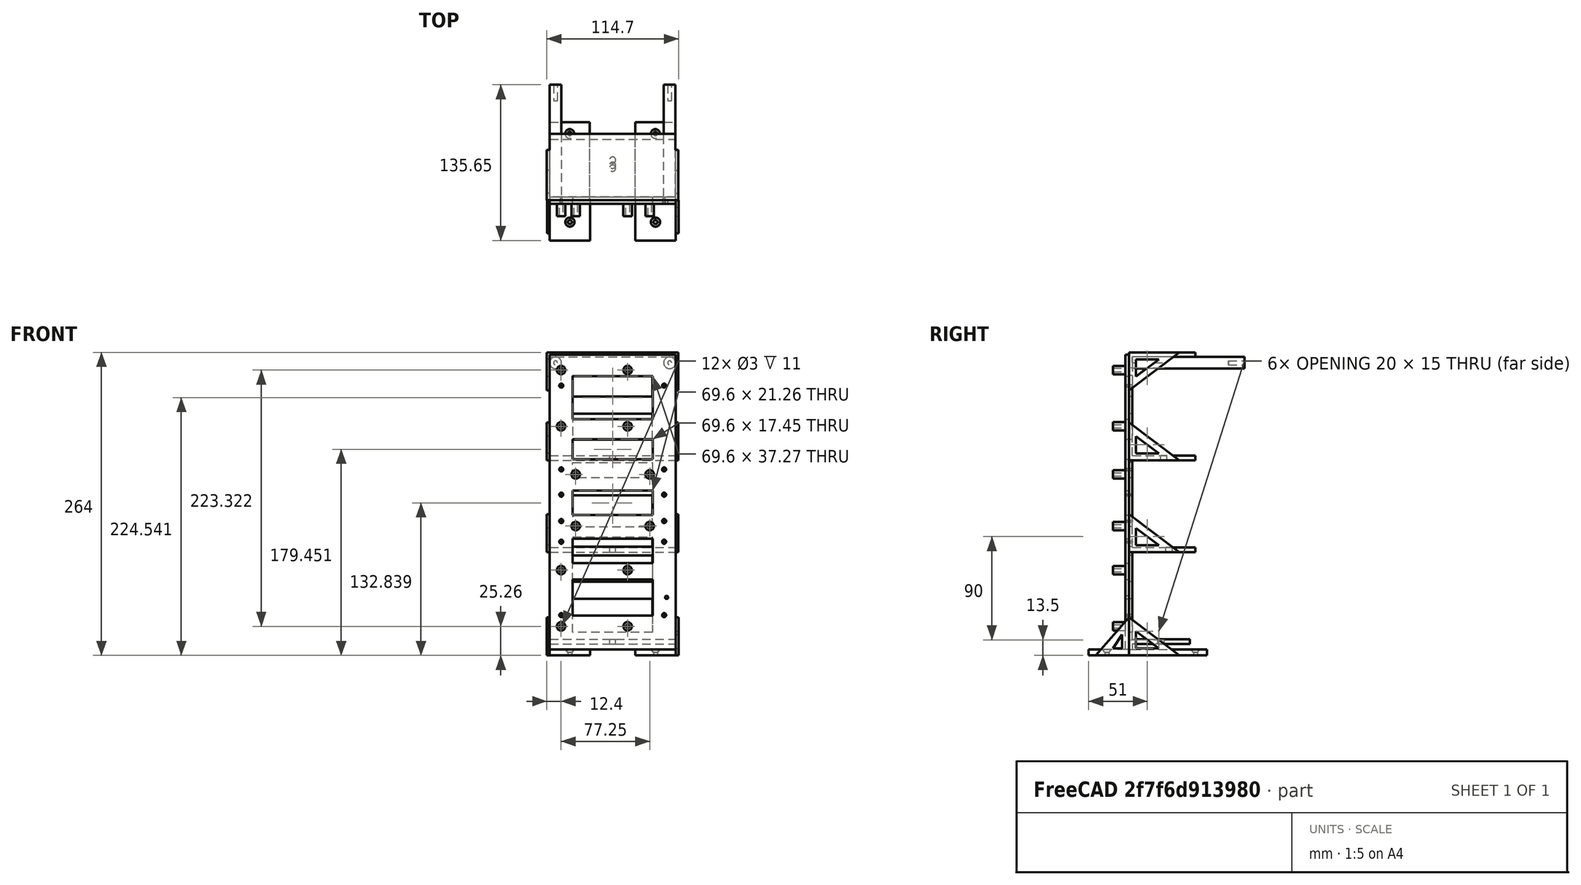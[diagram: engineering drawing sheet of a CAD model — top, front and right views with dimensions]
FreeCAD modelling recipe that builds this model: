
FCSTD DOCUMENT  (FreeCAD 1.0R39109 (Git))
Label: Tower
License: All rights reserved
LicenseURL: http://en.wikipedia.org/wiki/All_rights_reserved
objects: Sketcher::SketchObject×17, PartDesign::Pad×9, PartDesign::Plane×9, PartDesign::Pocket×4, App::Link×3, PartDesign::Hole×3, PartDesign::Mirrored×2, PartDesign::Body×2, App::Part×1
note: 97 computed .brp shape members not serialized (recipe doc carries the construction recipe); baked Part::Feature solids carry a one-line shape summary decoded from their .brp
EXTERNAL_REF file=../Master Document.FCStd obj=Spreadsheet
EXTERNAL_REF file=../../../Dev/PiTrac/3D Printed Parts/Enclosure Models/Combined Enclosure Model (DO NOT PRINT)/Connector Board.FCStd obj=GolfSim_Connector_Board_1
EXTERNAL_REF file=../../../Dev/PiTrac/3D Printed Parts/Enclosure Models/Combined Enclosure Model (DO NOT PRINT)/Pi 5.FCStd obj=RASPBERRY_PI_5_1

FEATURE [App::Link] Link  label="Monitor Chassis Parameters"
  LinkedObject = -> <external ../Master Document.FCStd>#Spreadsheet
FEATURE [Sketcher::SketchObject] Sketch  label="Backplate Sketch"
  ArcFitTolerance = 1e-06
  AttachmentSupport = -> [XZ_Plane001]
  FullyConstrained = false
  MakeInternals = false
  MapMode = 5
  Placement = pos=(0,0,0) rot=(1,0,0;1.5708rad)
  expr: Constraints[10] = <<Monitor Chassis Parameters>>.GSBackPlateBoltDiameter
  expr: Constraints[11] = <<Monitor Chassis Parameters>>.GSComputeBoardWidth / 2 - <<Monitor Chassis Parameters>>.GSBackPlateOuterHolesInsetFromSide
  expr: Constraints[15] = <<Monitor Chassis Parameters>>.GSBackPlateWidthIncrement
  expr: Constraints[55] = <<Monitor Chassis Parameters>>.GSBackPlateLengthIncrement
  expr: Constraints[59] = <<Monitor Chassis Parameters>>.GSBackPlateWidth
  expr: Constraints[71] = <<Monitor Chassis Parameters>>.GSBackPlateMinimumSpanWidth
  expr: Constraints[72] = <<Monitor Chassis Parameters>>.GSBackPlateMinimumSpanWidth
  expr: Constraints[7] = <<Monitor Chassis Parameters>>.GSComputeBoardHeight
  expr: Constraints[80] = <<Monitor Chassis Parameters>>.GSBackPlateLengthIncrement
  expr: Constraints[8] = <<Monitor Chassis Parameters>>.GSComputeBoardWidth
  expr: Constraints[9] = <<Monitor Chassis Parameters>>.GSComputeBoardWidth / 2
  sketch-geometry (33):
    g0: LineSegment [constr] StartX=-50.8 StartY=24.4067 StartZ=0 EndX=50.8 EndY=24.4067 EndZ=0
    g1: LineSegment [constr] StartX=50.8 StartY=24.4067 StartZ=0 EndX=50.8 EndY=253.007 EndZ=0
    g2: LineSegment [constr] StartX=50.8 StartY=253.007 StartZ=0 EndX=-50.8 EndY=253.007 EndZ=0
    g3: LineSegment [constr] StartX=-50.8 StartY=253.007 StartZ=0 EndX=-50.8 EndY=24.4067 EndZ=0
    g4: Circle CenterX=46.99 CenterY=45.5 CenterZ=0 NormalX=0 NormalY=0 NormalZ=1 AngleXU=0 Radius=1.4
    g5: LineSegment StartX=-54.8 StartY=257.007 StartZ=0 EndX=-54.8 EndY=20.4067 EndZ=0
    g6: LineSegment [constr] StartX=-54.8 StartY=20.4067 StartZ=0 EndX=54.8 EndY=20.4067 EndZ=0
    g7: LineSegment StartX=34.8 StartY=117.208 StartZ=0 EndX=-34.8 EndY=117.208 EndZ=0
    g8: LineSegment StartX=-34.8 StartY=117.208 StartZ=0 EndX=-34.8 EndY=138.47 EndZ=0
    g9: LineSegment StartX=-34.8 StartY=138.47 StartZ=0 EndX=34.8 EndY=138.47 EndZ=0
    g10: LineSegment StartX=34.8 StartY=138.47 StartZ=0 EndX=34.8 EndY=117.208 EndZ=0
    g11: LineSegment StartX=34.8 StartY=238.176 StartZ=0 EndX=-34.8 EndY=238.176 EndZ=0
    g12: LineSegment StartX=-34.8 StartY=238.176 StartZ=0 EndX=-34.8 EndY=200.906 EndZ=0
    g13: LineSegment StartX=-34.8 StartY=200.906 StartZ=0 EndX=34.8 EndY=200.906 EndZ=0
    g14: LineSegment StartX=34.8 StartY=200.906 StartZ=0 EndX=34.8 EndY=238.176 EndZ=0
    g15: LineSegment StartX=-34.8 StartY=183.174 StartZ=0 EndX=-34.8 EndY=165.729 EndZ=0
    g16: LineSegment StartX=-34.8 StartY=165.729 StartZ=0 EndX=34.8 EndY=165.729 EndZ=0
    g17: LineSegment StartX=34.8 StartY=165.729 StartZ=0 EndX=34.8 EndY=183.174 EndZ=0
    g18: LineSegment StartX=34.8 StartY=183.174 StartZ=0 EndX=-34.8 EndY=183.174 EndZ=0
    g19: LineSegment StartX=-34.8 StartY=96.4911 StartZ=0 EndX=-34.8 EndY=75.4807 EndZ=0
    g20: LineSegment StartX=-34.8 StartY=75.4807 StartZ=0 EndX=34.8 EndY=75.4807 EndZ=0
    g21: LineSegment StartX=34.8 StartY=75.4807 StartZ=0 EndX=34.8 EndY=96.4911 EndZ=0
    g22: LineSegment StartX=34.8 StartY=96.4911 StartZ=0 EndX=-34.8 EndY=96.4911 EndZ=0
    g23: LineSegment StartX=-34.8 StartY=61.1974 StartZ=0 EndX=-34.8 EndY=29.6985 EndZ=0
    g24: LineSegment StartX=34.8 StartY=29.6985 StartZ=0 EndX=34.8 EndY=61.1974 EndZ=0
    g25: LineSegment StartX=54.8 StartY=20.4067 StartZ=0 EndX=54.8 EndY=257.007 EndZ=0
    g26: LineSegment StartX=-54.8 StartY=257.007 StartZ=0 EndX=54.8 EndY=257.007 EndZ=0
    g27: LineSegment StartX=-54.8 StartY=20.4067 StartZ=0 EndX=-54.8 EndY=0 EndZ=0
    g28: LineSegment StartX=-54.8 StartY=0 StartZ=0 EndX=54.8 EndY=0 EndZ=0
    g29: LineSegment StartX=54.8 StartY=0 StartZ=0 EndX=54.8 EndY=20.4067 EndZ=0
    g30: LineSegment [constr] StartX=54.8 StartY=20.4067 StartZ=0 EndX=-54.8 EndY=20.4067 EndZ=0
    g31: LineSegment StartX=-34.8 StartY=61.1974 StartZ=0 EndX=34.8 EndY=61.1974 EndZ=0
    g32: LineSegment StartX=-34.8 StartY=29.6985 StartZ=0 EndX=34.8 EndY=29.6985 EndZ=0
  constraints (86):
    c: Coincident(g0,g1)
    c: Coincident(g1,g2)
    c: Coincident(g2,g3)
    c: Coincident(g3,g0)
    c: Horizontal(g2)
    c: Vertical(g1)
    c: Vertical(g3)
    c: DistanceY(g0,g2) = 228.6
    c: DistanceX(g0,g0) = 101.6
    c: DistanceX(g0,g-1) = 50.8
    c: Diameter(g4) = 2.8
    c: DistanceX(g-1,g4) = 46.99
    c: Coincident(g5,g6)
    c: Vertical(g5)
    c: Horizontal(g6)
    c: DistanceX(g5,g0) = 4
    c: Horizontal(g0)
    c: Coincident(g7,g8)
    c: Coincident(g8,g9)
    c: Coincident(g9,g10)
    c: Coincident(g10,g7)
    c: Horizontal(g7)
    c: Vertical(g8)
    c: Vertical(g10)
    c: Coincident(g11,g12)
    c: Coincident(g12,g13)
    c: Coincident(g13,g14)
    c: Coincident(g14,g11)
    c: Horizontal(g11)
    c: Horizontal(g13)
    c: Vertical(g12)
    c: Vertical(g14)
    c: Coincident(g15,g16)
    c: Coincident(g16,g17)
    c: Coincident(g17,g18)
    c: Coincident(g18,g15)
    c: Vertical(g15)
    c: Vertical(g17)
    c: Horizontal(g16)
    c: Coincident(g19,g20)
    c: Coincident(g20,g21)
    c: Coincident(g21,g22)
    c: Coincident(g22,g19)
    c: Vertical(g19)
    c: Vertical(g21)
    c: Horizontal(g20)
    c: Horizontal(g22)
    c: Vertical(g23)
    c: Vertical(g24)
    c: Vertical(g15,g19)
    c: Vertical(g19,g23)
    c: Vertical(g7,g21)
    c: Vertical(g21,g24)
    c: Coincident(g25,g6)
    c: Vertical(g25)
    c: DistanceY(g1,g25) = 4
    c: Horizontal(g5,g25)
    c: Coincident(g26,g5)
    c: Coincident(g26,g25)
    c: DistanceX(g5,g6) = 109.6
    c: Coincident(g27,g28)
    c: Coincident(g28,g29)
    c: Coincident(g29,g30)
    c: Coincident(g30,g27)
    c: Vertical(g27)
    c: Vertical(g29)
    c: Horizontal(g28)
    c: Horizontal(g30)
    c: Coincident(g27,g5)
    c: Horizontal(g28,g-1)
    c: Vertical(g29,g6)
    c: DistanceX(g5,g11) = 20
    c: DistanceX(g11,g25) = 20
    c: Horizontal(g9)
    c: Coincident(g31,g23)
    c: Coincident(g31,g24)
    c: Horizontal(g31)
    c: Vertical(g11,g15)
    c: Vertical(g11,g9)
    c: Vertical(g16,g9)
    c: DistanceY(g5,g0) = 4
    c: Coincident(g32,g23)
    c: Coincident(g32,g24)
    c: Horizontal(g32)
    c: Horizontal(g18)
    c: Vertical(g15,g8)
FEATURE [PartDesign::Pad] Pad  label="Backplate Pad"
  Direction = (0,-1,2e-16)
  Length = 3
  Length2 = 10
  Placement = pos=(0,0,0) rot=(1,0,0;1.5708rad)
  Profile = -> Sketch
  ReferenceAxis = -> Sketch [N_Axis]
  Reversed = true
  Suppressed = false
  Type = 0
  expr: Length = <<Monitor Chassis Parameters>>.GSBackPlateThickness
FEATURE [Sketcher::SketchObject] Sketch001  label="Backplate Risers Sketch"
  ArcFitTolerance = 1e-06
  AttachmentSupport = -> [XZ_Plane001]
  FullyConstrained = false
  MakeInternals = false
  MapMode = 5
  Placement = pos=(0,0,0) rot=(1,0,0;1.5708rad)
  expr: Constraints[10] = <<Monitor Chassis Parameters>>.GsPi5MountingHoleDiameter
  expr: Constraints[11] = <<Monitor Chassis Parameters>>.GsPi5MountingHoleDiameter
  expr: Constraints[12] = <<Monitor Chassis Parameters>>.GsPi5MountingHoleDiameter
  expr: Constraints[13] = <<Monitor Chassis Parameters>>.GsPi5MountingHoleDiameter
  expr: Constraints[18] = <<Monitor Chassis Parameters>>.GSBackPlateScrewHoleDiameter + 2 * <<Monitor Chassis Parameters>>.GSBackPlateStandoffWallThickness
  expr: Constraints[20] = <<Monitor Chassis Parameters>>.GSBackPlateScrewHoleDiameter + 2 * <<Monitor Chassis Parameters>>.GSBackPlateStandoffWallThickness
  expr: Constraints[26] = <<Monitor Chassis Parameters>>.GSBackPlateScrewHoleDiameter + 2 * <<Monitor Chassis Parameters>>.GSBackPlateStandoffWallThickness
  expr: Constraints[27] = <<Monitor Chassis Parameters>>.GSBackPlateScrewHoleDiameter + 2 * <<Monitor Chassis Parameters>>.GSBackPlateStandoffWallThickness
  expr: Constraints[28] = <<Monitor Chassis Parameters>>.GSBackPlateScrewHoleDiameter + 2 * <<Monitor Chassis Parameters>>.GSBackPlateStandoffWallThickness
  expr: Constraints[29] = <<Monitor Chassis Parameters>>.GSBackPlateScrewHoleDiameter + 2 * <<Monitor Chassis Parameters>>.GSBackPlateStandoffWallThickness
  expr: Constraints[30] = <<Monitor Chassis Parameters>>.GSBackPlateScrewHoleDiameter + 2 * <<Monitor Chassis Parameters>>.GSBackPlateStandoffWallThickness
  expr: Constraints[32] = <<Monitor Chassis Parameters>>.GSBackPlateVerticalOffset
  expr: Constraints[34] = <<Monitor Chassis Parameters>>.GSPi5MountingHoleCenterLength
  expr: Constraints[36] = <<Monitor Chassis Parameters>>.GSPi5MountingHoleCenterWidth
  expr: Constraints[38] = <<Monitor Chassis Parameters>>.GSPi5MountingHoleCenterWidth
  expr: Constraints[41] = <<Monitor Chassis Parameters>>.GsPi5MountingHoleDiameter
  expr: Constraints[58] = <<Monitor Chassis Parameters>>.GSMonitorConnectorBoardHoleSeparationLength
  expr: Constraints[59] = <<Monitor Chassis Parameters>>.GSMonitorConnectorBoardHoleSeparationWidth
  expr: Constraints[60] = 0.5 * <<Monitor Chassis Parameters>>.GSMonitorConnectorBoardHoleSeparationLength
  expr: Constraints[61] = <<Monitor Chassis Parameters>>.GSPi5MountingHoleCenterLength
  expr: Constraints[6] = <<Monitor Chassis Parameters>>.GSComputeBoardWidth / 2
  expr: Constraints[7] = <<Monitor Chassis Parameters>>.GsPi5MountingHoleDiameter
  expr: Constraints[8] = <<Monitor Chassis Parameters>>.GsPi5MountingHoleDiameter
  expr: Constraints[9] = <<Monitor Chassis Parameters>>.GsPi5MountingHoleDiameter
  sketch-geometry (28):
    g0: LineSegment [constr] StartX=-50.8 StartY=20 StartZ=0 EndX=50.8 EndY=20 EndZ=0
    g1: LineSegment [constr] StartX=50.8 StartY=20 StartZ=0 EndX=50.8 EndY=248.6 EndZ=0
    g2: LineSegment [constr] StartX=50.8 StartY=248.6 StartZ=0 EndX=-50.8 EndY=248.6 EndZ=0
    g3: LineSegment [constr] StartX=-50.8 StartY=248.6 StartZ=0 EndX=-50.8 EndY=20 EndZ=0
    g4: Circle CenterX=-45 CenterY=243.582 CenterZ=0 NormalX=0 NormalY=0 NormalZ=1 AngleXU=0 Radius=1.5
    g5: Circle CenterX=13 CenterY=243.582 CenterZ=0 NormalX=0 NormalY=0 NormalZ=1 AngleXU=0 Radius=1.5
    g6: Circle CenterX=-45 CenterY=20.2601 CenterZ=0 NormalX=0 NormalY=0 NormalZ=1 AngleXU=0 Radius=1.5
    g7: Circle CenterX=13 CenterY=20.2601 CenterZ=0 NormalX=0 NormalY=0 NormalZ=1 AngleXU=0 Radius=1.5
    g8: Circle CenterX=-45 CenterY=69.2601 CenterZ=0 NormalX=0 NormalY=0 NormalZ=1 AngleXU=0 Radius=1.5
    g9: Circle CenterX=-45 CenterY=194.582 CenterZ=0 NormalX=0 NormalY=0 NormalZ=1 AngleXU=0 Radius=1.5
    g10: Circle CenterX=13 CenterY=194.582 CenterZ=0 NormalX=0 NormalY=0 NormalZ=1 AngleXU=0 Radius=1.5
    g11: Circle CenterX=-45 CenterY=243.582 CenterZ=0 NormalX=0 NormalY=0 NormalZ=1 AngleXU=0 Radius=3.7
    g12: Circle CenterX=13 CenterY=243.582 CenterZ=0 NormalX=0 NormalY=0 NormalZ=1 AngleXU=0 Radius=3.7
    g13: Circle CenterX=-45 CenterY=194.582 CenterZ=0 NormalX=0 NormalY=0 NormalZ=1 AngleXU=0 Radius=3.7
    g14: Circle CenterX=13 CenterY=194.582 CenterZ=0 NormalX=0 NormalY=0 NormalZ=1 AngleXU=0 Radius=3.7
    g15: Circle CenterX=-45 CenterY=69.2601 CenterZ=0 NormalX=0 NormalY=0 NormalZ=1 AngleXU=0 Radius=3.7
    g16: Circle CenterX=-45 CenterY=20.2601 CenterZ=0 NormalX=0 NormalY=0 NormalZ=1 AngleXU=0 Radius=3.7
    g17: Circle CenterX=13 CenterY=20.2601 CenterZ=0 NormalX=0 NormalY=0 NormalZ=1 AngleXU=0 Radius=3.7
    g18: Circle CenterX=13 CenterY=69.2601 CenterZ=0 NormalX=0 NormalY=0 NormalZ=1 AngleXU=0 Radius=3.7
    g19: Circle CenterX=13 CenterY=69.2601 CenterZ=0 NormalX=0 NormalY=0 NormalZ=1 AngleXU=0 Radius=1.5
    g20: Circle CenterX=-32.25 CenterY=107.639 CenterZ=0 NormalX=0 NormalY=0 NormalZ=1 AngleXU=0 Radius=1.5
    g21: Circle CenterX=-32.25 CenterY=107.639 CenterZ=0 NormalX=0 NormalY=0 NormalZ=1 AngleXU=0 Radius=3.7
    g22: Circle CenterX=32.25 CenterY=107.639 CenterZ=0 NormalX=0 NormalY=0 NormalZ=1 AngleXU=0 Radius=1.5
    g23: Circle CenterX=32.25 CenterY=107.639 CenterZ=0 NormalX=0 NormalY=0 NormalZ=1 AngleXU=0 Radius=3.7
    g24: Circle CenterX=32.25 CenterY=152.639 CenterZ=0 NormalX=0 NormalY=0 NormalZ=1 AngleXU=0 Radius=1.5
    g25: Circle CenterX=32.25 CenterY=152.639 CenterZ=0 NormalX=0 NormalY=0 NormalZ=1 AngleXU=0 Radius=3.7
    g26: Circle CenterX=-32.25 CenterY=152.639 CenterZ=0 NormalX=0 NormalY=0 NormalZ=1 AngleXU=0 Radius=1.5
    g27: Circle CenterX=-32.25 CenterY=152.639 CenterZ=0 NormalX=0 NormalY=0 NormalZ=1 AngleXU=0 Radius=3.7
  constraints (65):
    c: Coincident(g0,g1)
    c: Coincident(g1,g2)
    c: Coincident(g2,g3)
    c: Coincident(g3,g0)
    c: Vertical(g1)
    c: Vertical(g3)
    c: DistanceX(g0,g-1) = 50.8
    c: Diameter(g4) = 3
    c: Diameter(g5) = 3
    c: Diameter(g6) = 3
    c: Diameter(g7) = 3
    c: Diameter(g8) = 3
    c: Diameter(g9) = 3
    c: Diameter(g10) = 3
    c: Horizontal(g0)
    c: Vertical(g5,g10)
    c: Horizontal(g5,g4)
    c: Coincident(g11,g4)
    c: Diameter(g11) = 7.4
    c: Coincident(g12,g5)
    c: Diameter(g12) = 7.4
    c: Coincident(g13,g9)
    c: Coincident(g14,g10)
    c: Coincident(g15,g8)
    c: Coincident(g16,g6)
    c: Coincident(g17,g7)
    c: Diameter(g17) = 7.4
    c: Diameter(g16) = 7.4
    c: Diameter(g15) = 7.4
    c: Diameter(g14) = 7.4
    c: Diameter(g13) = 7.4
    c: Horizontal(g7,g6)
    c: DistanceY(g-1,g0) = 20
    c: Horizontal(g2,g1)
    c: DistanceX(g4,g5) = 58
    c: Horizontal(g9,g10)
    c: DistanceY(g9,g4) = 49
    c: Vertical(g8,g6)
    c: DistanceY(g6,g8) = 49
    c: Diameter(g18) = 7.4
    c: Coincident(g19,g18)
    c: Diameter(g19) = 3
    c: Horizontal(g18,g8)
    c: Vertical(g18,g7)
    c: Coincident(g21,g20)
    c: Diameter(g21) = 7.4
    c: Diameter(g20) = 3
    c: Coincident(g23,g22)
    c: Diameter(g23) = 7.4
    c: Diameter(g22) = 3
    c: Coincident(g25,g24)
    c: Diameter(g25) = 7.4
    c: Diameter(g24) = 3
    c: Coincident(g27,g26)
    c: Diameter(g27) = 7.4
    c: Diameter(g26) = 3
    c: Horizontal(g24,g26)
    c: Horizontal(g22,g20)
    c: DistanceX(g26,g24) = 64.5
    c: DistanceY(g20,g26) = 45
    c: DistanceX(g26,g-1) = 32.25
    c: DistanceX(g8,g18) = 58
    c: DistanceX(g6,g-1) = 45
    c: Vertical(g8,g9)
    c: Vertical(g10,g7)
FEATURE [PartDesign::Pad] Pad001  label="Backplate Risers Pad"
  BaseFeature = -> Pad
  Direction = (0,-1,2e-16)
  Length = 11
  Length2 = 10
  Placement = pos=(0,0,0) rot=(1,0,0;1.5708rad)
  Profile = -> Sketch001
  ReferenceAxis = -> Sketch001 [N_Axis]
  Suppressed = false
  Type = 0
  expr: Length = <<Monitor Chassis Parameters>>.GSBackPlateStandoffHeight
FEATURE [Sketcher::SketchObject] Sketch002  label="Backplate Foot Sketch"
  ArcFitTolerance = 1e-06
  AttachmentSupport = -> [XZ_Plane001]
  FullyConstrained = true
  MakeInternals = false
  MapMode = 5
  Placement = pos=(0,0,0) rot=(1,0,0;1.5708rad)
  expr: Constraints[11] = <<Monitor Chassis Parameters>>.GSTowerFeetThickness
  expr: Constraints[21] = <<Monitor Chassis Parameters>>.GSTowerFeetThickness
  expr: Constraints[22] = <<Monitor Chassis Parameters>>.GSBackPlateFootWidth
  expr: Constraints[23] = 0.5 * <<Monitor Chassis Parameters>>.GSBackPlateWidth
  expr: Constraints[8] = <<Monitor Chassis Parameters>>.GSBackPlateFootWidth
  expr: Constraints[9] = 0.5 * <<Monitor Chassis Parameters>>.GSBackPlateWidth
  sketch-geometry (8):
    g0: LineSegment StartX=-54.8 StartY=-5 StartZ=0 EndX=-19.8 EndY=-5 EndZ=0
    g1: LineSegment StartX=-19.8 StartY=-5 StartZ=0 EndX=-19.8 EndY=0 EndZ=0
    g2: LineSegment StartX=-19.8 StartY=0 StartZ=0 EndX=-54.8 EndY=0 EndZ=0
    g3: LineSegment StartX=-54.8 StartY=0 StartZ=0 EndX=-54.8 EndY=-5 EndZ=0
    g4: LineSegment StartX=54.8 StartY=-5 StartZ=0 EndX=54.8 EndY=0 EndZ=0
    g5: LineSegment StartX=54.8 StartY=0 StartZ=0 EndX=19.8 EndY=0 EndZ=0
    g6: LineSegment StartX=19.8 StartY=0 StartZ=0 EndX=19.8 EndY=-5 EndZ=0
    g7: LineSegment StartX=19.8 StartY=-5 StartZ=0 EndX=54.8 EndY=-5 EndZ=0
  constraints (24):
    c: Coincident(g0,g1)
    c: Coincident(g1,g2)
    c: Coincident(g2,g3)
    c: Coincident(g3,g0)
    c: Horizontal(g0)
    c: Horizontal(g2)
    c: Vertical(g1)
    c: Vertical(g3)
    c: DistanceX(g2,g1) = 35
    c: DistanceX(g2,g-1) = 54.8
    c: Horizontal(g2,g-1)
    c: DistanceY(g0,g2) = 5
    c: Coincident(g4,g5)
    c: Coincident(g5,g6)
    c: Coincident(g6,g7)
    c: Coincident(g7,g4)
    c: Vertical(g4)
    c: Vertical(g6)
    c: Horizontal(g5)
    c: Horizontal(g7)
    c: Horizontal(g5,g-1)
    c: DistanceY(g4,g4) = 5
    c: DistanceX(g6,g4) = 35
    c: DistanceX(g-1,g4) = 54.8
FEATURE [PartDesign::Pad] Pad002  label="Backplate Foot Pad"
  BaseFeature = -> Pad001
  Direction = (0,-1,2e-16)
  Length = 32
  Length2 = 3
  Placement = pos=(0,0,0) rot=(1,0,0;1.5708rad)
  Profile = -> Sketch002
  ReferenceAxis = -> Sketch002 [N_Axis]
  Suppressed = false
  Type = 4
  expr: Length = <<Monitor Chassis Parameters>>.GSBackPlateFootLengthBackward
  expr: Length2 = <<Monitor Chassis Parameters>>.GSBackPlateThickness
FEATURE [Sketcher::SketchObject] Sketch003  label="Backplate Foot Screw Holes Sketch"
  ArcFitTolerance = 1e-06
  AttachmentSupport = -> [XY_Plane001]
  FullyConstrained = true
  MakeInternals = false
  MapMode = 5
  expr: Constraints[0] = 0.5 * <<Monitor Chassis Parameters>>.GSBackPlateFootLengthBackward
  expr: Constraints[1] = 0.5 * <<Monitor Chassis Parameters>>.GSBackPlateWidth - 0.5 * <<Monitor Chassis Parameters>>.GSBackPlateFootWidth
  expr: Constraints[2] = 0.5 * <<Monitor Chassis Parameters>>.GSBackPlateWidth - 0.5 * <<Monitor Chassis Parameters>>.GSBackPlateFootWidth
  expr: Constraints[3] = <<Monitor Chassis Parameters>>.GSTowerFeetScrewDiameter
  expr: Constraints[4] = <<Monitor Chassis Parameters>>.GSTowerFeetScrewDiameter
  sketch-geometry (2):
    g0: Circle CenterX=-37.3 CenterY=-16 CenterZ=0 NormalX=0 NormalY=0 NormalZ=1 AngleXU=0 Radius=1.7
    g1: Circle CenterX=37.3 CenterY=-16 CenterZ=0 NormalX=0 NormalY=0 NormalZ=1 AngleXU=0 Radius=1.7
  constraints (6):
    c: DistanceY(g0,g-1) = 16
    c: DistanceX(g0,g-1) = 37.3
    c: DistanceX(g-1,g1) = 37.3
    c: Diameter(g0) = 3.4
    c: Diameter(g1) = 3.4
    c: Horizontal(g1,g0)
FEATURE [PartDesign::Hole] Hole  label="Backplate Foot Screw Holes"
  BaseFeature = -> Pad002
  CustomThreadClearance = 0
  Depth = 25
  DepthType = 0
  Diameter = 3.4
  DrillForDepth = false
  DrillPoint = 1
  DrillPointAngle = 118
  HoleCutCountersinkAngle = 90
  HoleCutCustomValues = false
  HoleCutDepth = 0
  HoleCutDiameter = 8
  HoleCutType = 2
  ModelThread = false
  Placement = pos=(0,0,0) rot=(1,0,0;1.5708rad)
  Profile = -> Sketch003
  Suppressed = false
  Tapered = false
  TaperedAngle = 90
  ThreadClass = 0
  ThreadDepth = 25
  ThreadDepthType = 0
  ThreadDirection = 0
  ThreadFit = 0
  ThreadSize = 0
  ThreadType = 0
  Threaded = false
  UseCustomThreadClearance = false
  expr: Diameter = <<Monitor Chassis Parameters>>.GSTowerFeetScrewDiameter
  expr: HoleCutDiameter = <<Monitor Chassis Parameters>>.GSM4BoltCountersinkDiameter
FEATURE [PartDesign::Plane] DatumPlane
  AttachmentOffset = pos=(0,0,54.8) rot=(0,0,1;0rad)
  AttachmentSupport = -> [YZ_Plane001]
  Length = 82.357
  MapMode = 5
  Placement = pos=(54.8,0,0) rot=(0.57735,0.57735,0.57735;2.0944rad)
  ResizeMode = 0
  Width = 307.364
  expr: .AttachmentOffset.Base.z = 0.5 * <<Monitor Chassis Parameters>>.GSBackPlateWidth
FEATURE [Sketcher::SketchObject] Sketch004  label="Foot Support Corner Sketch"
  ArcFitTolerance = 1e-06
  AttachmentSupport = -> [DatumPlane]
  FullyConstrained = true
  MakeInternals = false
  MapMode = 5
  Placement = pos=(54.8,0,0) rot=(0.57735,0.57735,0.57735;2.0944rad)
  expr: Constraints[14] = <<Monitor Chassis Parameters>>.GSSideCornerCutoutInset
  expr: Constraints[15] = <<Monitor Chassis Parameters>>.GSSideCornerCutoutInset
  expr: Constraints[16] = 2.5 * <<Monitor Chassis Parameters>>.GSSideCornerCutoutInset
  expr: Constraints[17] = 2.5 * <<Monitor Chassis Parameters>>.GSSideCornerCutoutInset
  expr: Constraints[1] = <<Monitor Chassis Parameters>>.GSBackPlateThickness
  expr: Constraints[4] = <<Monitor Chassis Parameters>>.GSTowerFeetThickness
  expr: Constraints[7] = 0.9 * <<Monitor Chassis Parameters>>.GSBackPlateFootLengthBackward
  expr: Constraints[8] = 0.6 * <<Monitor Chassis Parameters>>.GSTowerFloorDepth
  sketch-geometry (6):
    g0: LineSegment StartX=-25.8 StartY=-5 StartZ=0 EndX=3 EndY=-5 EndZ=0
    g1: LineSegment StartX=3 StartY=28 StartZ=0 EndX=3 EndY=-5 EndZ=0
    g2: LineSegment StartX=-25.8 StartY=-5 StartZ=0 EndX=3 EndY=28 EndZ=0
    g3: LineSegment StartX=-10.8 StartY=1 StartZ=0 EndX=-3 EndY=13 EndZ=0
    g4: LineSegment StartX=-3 StartY=13 StartZ=0 EndX=-3 EndY=1 EndZ=0
    g5: LineSegment StartX=-10.8 StartY=1 StartZ=0 EndX=-3 EndY=1 EndZ=0
  constraints (18):
    c: Horizontal(g0)
    c: DistanceX(g-1,g0) = 3
    c: Coincident(g1,g0)
    c: Vertical(g1)
    c: DistanceY(g0,g-1) = 5
    c: Coincident(g2,g0)
    c: Coincident(g2,g1)
    c: DistanceX(g0,g0) = 28.8
    c: DistanceY(g0,g1) = 33
    c: Coincident(g4,g3)
    c: Vertical(g4)
    c: Coincident(g5,g3)
    c: Coincident(g5,g4)
    c: Horizontal(g5)
    c: DistanceY(g0,g4) = 6
    c: DistanceX(g4,g0) = 6
    c: DistanceX(g0,g3) = 15
    c: DistanceY(g3,g1) = 15
FEATURE [PartDesign::Pad] Pad003  label="Foot Support Corner Pad"
  BaseFeature = -> Hole
  Direction = (1,0,0)
  Length = 2.5
  Length2 = 10
  Placement = pos=(0,0,0) rot=(1,0,0;1.5708rad)
  Profile = -> Sketch004
  ReferenceAxis = -> Sketch004 [N_Axis]
  Suppressed = false
  Type = 0
  expr: Length = <<Monitor Chassis Parameters>>.GSSideCornerThickness
FEATURE [PartDesign::Mirrored] Mirrored  label="Foot Support Corner Mirrored"
  BaseFeature = -> Pad003
  MirrorPlane = -> YZ_Plane001
  Originals = -> [Pad003]
  Placement = pos=(0,0,0) rot=(1,0,0;1.5708rad)
  Suppressed = false
  TransformMode = 0
FEATURE [PartDesign::Plane] DatumPlane001
  AttachmentOffset = pos=(0,0,54.8) rot=(0,0,1;0rad)
  AttachmentSupport = -> [YZ_Plane002]
  Length = 121.975
  MapMode = 5
  Placement = pos=(54.8,0,0) rot=(0.57735,0.57735,0.57735;2.0944rad)
  ResizeMode = 0
  Width = 315.975
  expr: .AttachmentOffset.Base.z = 0.5 * <<Monitor Chassis Parameters>>.GSBackPlateWidth
FEATURE [Sketcher::SketchObject] Sketch005  label="Frontplate Sketch"
  ArcFitTolerance = 1e-06
  AttachmentSupport = -> [XZ_Plane002]
  FullyConstrained = false
  MakeInternals = false
  MapMode = 5
  Placement = pos=(0,0,0) rot=(1,0,0;1.5708rad)
  expr: Constraints[105] = <<Monitor Chassis Parameters>>.GSFrontPlateMinimumSpanWidth - 5
  expr: Constraints[106] = <<Monitor Chassis Parameters>>.GSTowerFourthFloorHeight + <<Monitor Chassis Parameters>>.GSTowerFloorThickness
  expr: Constraints[107] = <<Monitor Chassis Parameters>>.GSTowerLayerJoinScrewDiameter
  expr: Constraints[108] = <<Monitor Chassis Parameters>>.GSTowerLayerJoinScrewDiameter
  expr: Constraints[110] = <<Monitor Chassis Parameters>>.GSTowerLayerJoinScrewInset
  expr: Constraints[111] = <<Monitor Chassis Parameters>>.GSTowerLayerJoinScrewInset
  expr: Constraints[112] = <<Monitor Chassis Parameters>>.GSTowerLayerJoinScrewDiameter
  expr: Constraints[113] = <<Monitor Chassis Parameters>>.GSTowerLayerJoinScrewDiameter
  expr: Constraints[115] = <<Monitor Chassis Parameters>>.GSTowerLayerJoinScrewDiameter
  expr: Constraints[116] = <<Monitor Chassis Parameters>>.GSTowerLayerJoinScrewDiameter
  expr: Constraints[120] = <<Monitor Chassis Parameters>>.GSTowerLayerJoinScrewDiameter
  expr: Constraints[121] = <<Monitor Chassis Parameters>>.GSTowerLayerJoinScrewDiameter
  expr: Constraints[123] = <<Monitor Chassis Parameters>>.GSTowerLayerJoinScrewHeightFromFoot_1
  expr: Constraints[124] = <<Monitor Chassis Parameters>>.GSTowerLayerJoinScrewHeightFromFoot_3
  expr: Constraints[126] = <<Monitor Chassis Parameters>>.GSTowerLayerJoinScrewHeightFromFoot_4
  expr: Constraints[127] = <<Monitor Chassis Parameters>>.GSTowerLayerJoinScrewHeightFromFoot_5
  expr: Constraints[129] = <<Monitor Chassis Parameters>>.GSTowerLayerJoinScrewDiameter
  expr: Constraints[130] = <<Monitor Chassis Parameters>>.GSTowerLayerJoinScrewDiameter
  expr: Constraints[133] = <<Monitor Chassis Parameters>>.GSTowerLayerJoinScrewHeightFromFoot_6
  expr: Constraints[13] = <<Monitor Chassis Parameters>>.GSBackPlateWidthIncrement
  expr: Constraints[145] = <<Monitor Chassis Parameters>>.GSTowerLayerJoinScrewDiameter
  expr: Constraints[150] = <<Monitor Chassis Parameters>>.GSTowerLayerJoinScrewHeightFromFoot_2
  expr: Constraints[46] = <<Monitor Chassis Parameters>>.GSFrontPlateMinimumSpanWidth - 5
  expr: Constraints[48] = <<Monitor Chassis Parameters>>.GSFrontPlateMinimumSpanWidth
  expr: Constraints[65] = <<Monitor Chassis Parameters>>.GSFrontPlateMinimumSpanWidth - 5
  expr: Constraints[71] = <<Monitor Chassis Parameters>>.GSBackPlateLengthIncrement
  expr: Constraints[75] = <<Monitor Chassis Parameters>>.GSBackPlateWidth
  expr: Constraints[76] = <<Monitor Chassis Parameters>>.GSBackPlateVerticalOffset
  expr: Constraints[7] = <<Monitor Chassis Parameters>>.GSComputeBoardHeight
  expr: Constraints[8] = <<Monitor Chassis Parameters>>.GSComputeBoardWidth
  expr: Constraints[96] = <<Monitor Chassis Parameters>>.GSFrontPlateMinimumSpanWidth - 5
  expr: Constraints[97] = <<Monitor Chassis Parameters>>.GSFrontPlateMinimumSpanWidth
  expr: Constraints[98] = <<Monitor Chassis Parameters>>.GSFrontPlateMinimumSpanWidth
  expr: Constraints[9] = <<Monitor Chassis Parameters>>.GSComputeBoardWidth / 2
  sketch-geometry (55):
    g0: LineSegment [constr] StartX=-50.8 StartY=24 StartZ=0 EndX=50.8 EndY=24 EndZ=0
    g1: LineSegment [constr] StartX=50.8 StartY=24 StartZ=0 EndX=50.8 EndY=252.6 EndZ=0
    g2: LineSegment [constr] StartX=50.8 StartY=252.6 StartZ=0 EndX=-50.8 EndY=252.6 EndZ=0
    g3: LineSegment [constr] StartX=-50.8 StartY=252.6 StartZ=0 EndX=-50.8 EndY=24 EndZ=0
    g4: LineSegment StartX=-54.8 StartY=256.6 StartZ=0 EndX=-54.8 EndY=20 EndZ=0
    g5: LineSegment [constr] StartX=-54.8 StartY=20 StartZ=0 EndX=54.8 EndY=20 EndZ=0
    g6: LineSegment StartX=34.8 StartY=162.959 StartZ=0 EndX=-34.8 EndY=162.959 EndZ=0
    g7: LineSegment StartX=-34.8 StartY=162.959 StartZ=0 EndX=-34.8 EndY=149.512 EndZ=0
    g8: LineSegment StartX=-34.8 StartY=149.512 StartZ=0 EndX=34.8 EndY=149.512 EndZ=0
    g9: LineSegment StartX=34.8 StartY=149.512 StartZ=0 EndX=34.8 EndY=162.959 EndZ=0
    g10: LineSegment StartX=34.8 StartY=107.062 StartZ=0 EndX=-34.8 EndY=107.062 EndZ=0
    g11: LineSegment StartX=-34.8 StartY=107.062 StartZ=0 EndX=-34.8 EndY=134.512 EndZ=0
    g12: LineSegment StartX=-34.8 StartY=134.512 StartZ=0 EndX=34.8 EndY=134.512 EndZ=0
    g13: LineSegment StartX=34.8 StartY=134.512 StartZ=0 EndX=34.8 EndY=107.062 EndZ=0
    g14: LineSegment StartX=34.8 StartY=239 StartZ=0 EndX=-34.8 EndY=239 EndZ=0
    g15: LineSegment StartX=-34.8 StartY=239 StartZ=0 EndX=-34.8 EndY=220.485 EndZ=0
    g16: LineSegment StartX=-34.8 StartY=220.485 StartZ=0 EndX=34.8 EndY=220.485 EndZ=0
    g17: LineSegment StartX=34.8 StartY=220.485 StartZ=0 EndX=34.8 EndY=239 EndZ=0
    g18: LineSegment StartX=34.8 StartY=182.959 StartZ=0 EndX=-34.8 EndY=182.959 EndZ=0
    g19: LineSegment StartX=-34.8 StartY=182.959 StartZ=0 EndX=-34.8 EndY=205.485 EndZ=0
    g20: LineSegment StartX=-34.8 StartY=205.485 StartZ=0 EndX=34.8 EndY=205.485 EndZ=0
    g21: LineSegment StartX=34.8 StartY=205.485 StartZ=0 EndX=34.8 EndY=182.959 EndZ=0
    g22: LineSegment StartX=-34.8 StartY=81.9803 StartZ=0 EndX=-34.8 EndY=59.2632 EndZ=0
    g23: LineSegment StartX=-34.8 StartY=59.2632 StartZ=0 EndX=34.8 EndY=59.2632 EndZ=0
    g24: LineSegment StartX=34.8 StartY=59.2632 StartZ=0 EndX=34.8 EndY=81.9803 EndZ=0
    g25: LineSegment StartX=34.8 StartY=81.9803 StartZ=0 EndX=-34.8 EndY=81.9803 EndZ=0
    g26: LineSegment StartX=-34.8 StartY=44.2632 StartZ=0 EndX=-34.8 EndY=15 EndZ=0
    g27: LineSegment StartX=-34.8 StartY=15 StartZ=0 EndX=34.8 EndY=15 EndZ=0
    g28: LineSegment StartX=34.8 StartY=15 StartZ=0 EndX=34.8 EndY=44.2632 EndZ=0
    g29: LineSegment StartX=34.8 StartY=44.2632 StartZ=0 EndX=-34.8 EndY=44.2632 EndZ=0
    g30: LineSegment StartX=54.8 StartY=20 StartZ=0 EndX=54.8 EndY=256.6 EndZ=0
    g31: LineSegment [constr] StartX=-54.8 StartY=256.6 StartZ=0 EndX=54.8 EndY=256.6 EndZ=0
    g32: LineSegment StartX=-54.8 StartY=20 StartZ=0 EndX=-54.8 EndY=0 EndZ=0
    g33: LineSegment StartX=-54.8 StartY=0 StartZ=0 EndX=54.8 EndY=0 EndZ=0
    g34: LineSegment StartX=54.8 StartY=0 StartZ=0 EndX=54.8 EndY=20 EndZ=0
    g35: LineSegment [constr] StartX=54.8 StartY=20 StartZ=0 EndX=-54.8 EndY=20 EndZ=0
    g36: LineSegment StartX=-54.8 StartY=256.6 StartZ=0 EndX=-54.8 EndY=259 EndZ=0
    g37: LineSegment StartX=-54.8 StartY=259 StartZ=0 EndX=54.8 EndY=259 EndZ=0
    g38: LineSegment StartX=54.8 StartY=259 StartZ=0 EndX=54.8 EndY=256.6 EndZ=0
    g39: Circle CenterX=-44.8 CenterY=30 CenterZ=0 NormalX=0 NormalY=0 NormalZ=1 AngleXU=0 Radius=0.855
    g40: Circle CenterX=44.8 CenterY=30 CenterZ=0 NormalX=0 NormalY=0 NormalZ=1 AngleXU=0 Radius=0.855
    g41: Circle CenterX=-44.8 CenterY=112 CenterZ=0 NormalX=0 NormalY=0 NormalZ=1 AngleXU=0 Radius=0.855
    g42: Circle CenterX=44.8 CenterY=112 CenterZ=0 NormalX=0 NormalY=0 NormalZ=1 AngleXU=0 Radius=0.855
    g43: Circle CenterX=-44.8 CenterY=157 CenterZ=0 NormalX=0 NormalY=0 NormalZ=1 AngleXU=0 Radius=0.855
    g44: Circle CenterX=44.8 CenterY=157 CenterZ=0 NormalX=0 NormalY=0 NormalZ=1 AngleXU=0 Radius=0.855
    g45: Circle CenterX=-44.8 CenterY=135 CenterZ=0 NormalX=0 NormalY=0 NormalZ=1 AngleXU=0 Radius=0.855
    g46: Circle CenterX=44.8 CenterY=135 CenterZ=0 NormalX=0 NormalY=0 NormalZ=1 AngleXU=0 Radius=0.855
    g47: Circle CenterX=-44.8 CenterY=230 CenterZ=0 NormalX=0 NormalY=0 NormalZ=1 AngleXU=0 Radius=0.855
    g48: Circle CenterX=44.8 CenterY=230 CenterZ=0 NormalX=0 NormalY=0 NormalZ=1 AngleXU=0 Radius=0.855
    g49: LineSegment StartX=-34.8 StartY=89.607 StartZ=0 EndX=34.8 EndY=89.607 EndZ=0
    g50: LineSegment StartX=34.8 StartY=89.607 StartZ=0 EndX=34.8 EndY=98.0817 EndZ=0
    g51: LineSegment StartX=34.8 StartY=98.0817 StartZ=0 EndX=-34.8 EndY=98.0817 EndZ=0
    g52: LineSegment StartX=-34.8 StartY=98.0817 StartZ=0 EndX=-34.8 EndY=89.607 EndZ=0
    g53: Circle CenterX=-44.8 CenterY=94 CenterZ=0 NormalX=0 NormalY=0 NormalZ=1 AngleXU=0 Radius=0.855
    g54: Circle CenterX=44.8 CenterY=94 CenterZ=0 NormalX=0 NormalY=0 NormalZ=1 AngleXU=0 Radius=0.85
  constraints (151):
    c: Coincident(g0,g1)
    c: Coincident(g1,g2)
    c: Coincident(g2,g3)
    c: Coincident(g3,g0)
    c: Horizontal(g2)
    c: Vertical(g1)
    c: Vertical(g3)
    c: DistanceY(g0,g2) = 228.6
    c: DistanceX(g0,g0) = 101.6
    c: DistanceX(g0,g-1) = 50.8
    c: Coincident(g4,g5)
    c: Vertical(g4)
    c: Horizontal(g5)
    c: DistanceX(g4,g0) = 4
    c: Horizontal(g0)
    c: Coincident(g6,g7)
    c: Coincident(g7,g8)
    c: Coincident(g8,g9)
    c: Coincident(g9,g6)
    c: Horizontal(g6)
    c: Horizontal(g8)
    c: Vertical(g7)
    c: Vertical(g9)
    c: Coincident(g10,g11)
    c: Coincident(g11,g12)
    c: Coincident(g12,g13)
    c: Coincident(g13,g10)
    c: Horizontal(g10)
    c: Horizontal(g12)
    c: Vertical(g11)
    c: Vertical(g13)
    c: Coincident(g14,g15)
    c: Coincident(g15,g16)
    c: Coincident(g16,g17)
    c: Coincident(g17,g14)
    c: Horizontal(g14)
    c: Horizontal(g16)
    c: Vertical(g15)
    c: Vertical(g17)
    c: Coincident(g18,g19)
    c: Coincident(g19,g20)
    c: Coincident(g20,g21)
    c: Coincident(g21,g18)
    c: Horizontal(g18)
    c: Horizontal(g20)
    c: Vertical(g19)
    c: DistanceY(g20,g16) = 15
    c: Vertical(g12,g18)
    c: DistanceY(g6,g18) = 20
    c: Coincident(g22,g23)
    c: Coincident(g23,g24)
    c: Coincident(g24,g25)
    c: Coincident(g25,g22)
    c: Vertical(g22)
    c: Vertical(g24)
    c: Horizontal(g23)
    c: Horizontal(g25)
    c: Coincident(g26,g27)
    c: Coincident(g27,g28)
    c: Coincident(g28,g29)
    c: Coincident(g29,g26)
    c: Vertical(g26)
    c: Vertical(g28)
    c: Horizontal(g27)
    c: Horizontal(g29)
    c: DistanceY(g26,g22) = 15
    c: Vertical(g22,g26)
    c: Vertical(g10,g24)
    c: Vertical(g24,g28)
    c: Coincident(g30,g5)
    c: Vertical(g30)
    c: DistanceY(g1,g30) = 4
    c: Horizontal(g4,g30)
    c: Coincident(g31,g4)
    c: Coincident(g31,g30)
    c: DistanceX(g4,g5) = 109.6
    c: DistanceY(g-1,g5) = 20
    c: Coincident(g32,g33)
    c: Coincident(g33,g34)
    c: Coincident(g34,g35)
    c: Coincident(g35,g32)
    c: Vertical(g32)
    c: Vertical(g34)
    c: Horizontal(g33)
    c: Horizontal(g35)
    c: Coincident(g32,g4)
    c: Horizontal(g33,g-1)
    c: Vertical(g34,g5)
    c: Vertical(g21)
    c: Coincident(g36,g4)
    c: Vertical(g36)
    c: Coincident(g37,g36)
    c: Horizontal(g37)
    c: Coincident(g38,g37)
    c: Coincident(g38,g30)
    c: Vertical(g38)
    c: DistanceY(g-1,g26) = 15
    c: DistanceX(g32,g26) = 20
    c: DistanceX(g27,g33) = 20
    c: Vertical(g10,g22)
    c: Vertical(g11,g7)
    c: Vertical(g6,g18)
    c: Vertical(g19,g15)
    c: Vertical(g12,g8)
    c: Vertical(g20,g16)
    c: DistanceY(g12,g8) = 15
    c: DistanceY(g33,g37) = 259
    c: Diameter(g39) = 1.71
    c: Diameter(g40) = 1.71
    c: Horizontal(g40,g39)
    c: DistanceX(g4,g39) = 10
    c: DistanceX(g40,g5) = 10
    c: Diameter(g41) = 1.71
    c: Diameter(g42) = 1.71
    c: Horizontal(g42,g41)
    c: Diameter(g43) = 1.71
    c: Diameter(g44) = 1.71
    c: Horizontal(g44,g43)
    c: Vertical(g43,g39)
    c: Vertical(g44,g42)
    c: Diameter(g45) = 1.71
    c: Diameter(g46) = 1.71
    c: Horizontal(g46,g45)
    c: DistanceY(g-1,g39) = 30
    c: DistanceY(g-1,g41) = 112
    c: Vertical(g45,g41)
    c: DistanceY(g-1,g45) = 135
    c: DistanceY(g-1,g43) = 157
    c: Vertical(g42,g46)
    c: Diameter(g48) = 1.71
    c: Diameter(g47) = 1.71
    c: Vertical(g48,g44)
    c: Vertical(g47,g43)
    c: DistanceY(g-1,g47) = 230
    c: Horizontal(g48,g47)
    c: Coincident(g49,g50)
    c: Coincident(g50,g51)
    c: Coincident(g51,g52)
    c: Coincident(g52,g49)
    c: Horizontal(g49)
    c: Horizontal(g51)
    c: Vertical(g50)
    c: Vertical(g52)
    c: Vertical(g49,g22)
    c: Vertical(g49,g24)
    c: Diameter(g53) = 1.71
    c: Vertical(g41,g53)
    c: Diameter(g54) = 1.7
    c: Horizontal(g53,g54)
    c: Vertical(g54,g42)
    c: DistanceY(g-1,g53) = 94
FEATURE [PartDesign::Pad] Pad004  label="Frontplate Pad"
  Direction = (0,-1,2e-16)
  Length = 3
  Length2 = 10
  Placement = pos=(0,0,0) rot=(1,0,0;1.5708rad)
  Profile = -> Sketch005
  ReferenceAxis = -> Sketch005 [N_Axis]
  Reversed = true
  Suppressed = false
  Type = 0
  expr: Length = <<Monitor Chassis Parameters>>.GSBackPlateThickness
FEATURE [Sketcher::SketchObject] Sketch007  label="Frontplate Foot Sketch"
  ArcFitTolerance = 1e-06
  AttachmentSupport = -> [XZ_Plane002]
  FullyConstrained = true
  MakeInternals = false
  MapMode = 5
  Placement = pos=(0,0,0) rot=(1,0,0;1.5708rad)
  expr: Constraints[11] = <<Monitor Chassis Parameters>>.GSTowerFeetThickness
  expr: Constraints[21] = <<Monitor Chassis Parameters>>.GSTowerFeetThickness
  expr: Constraints[22] = <<Monitor Chassis Parameters>>.GSBackPlateFootWidth
  expr: Constraints[23] = 0.5 * <<Monitor Chassis Parameters>>.GSBackPlateWidth
  expr: Constraints[8] = <<Monitor Chassis Parameters>>.GSBackPlateFootWidth
  expr: Constraints[9] = 0.5 * <<Monitor Chassis Parameters>>.GSBackPlateWidth
  sketch-geometry (8):
    g0: LineSegment StartX=-54.8 StartY=-5 StartZ=0 EndX=-19.8 EndY=-5 EndZ=0
    g1: LineSegment StartX=-19.8 StartY=-5 StartZ=0 EndX=-19.8 EndY=0 EndZ=0
    g2: LineSegment StartX=-19.8 StartY=0 StartZ=0 EndX=-54.8 EndY=0 EndZ=0
    g3: LineSegment StartX=-54.8 StartY=0 StartZ=0 EndX=-54.8 EndY=-5 EndZ=0
    g4: LineSegment StartX=54.8 StartY=-5 StartZ=0 EndX=54.8 EndY=0 EndZ=0
    g5: LineSegment StartX=54.8 StartY=0 StartZ=0 EndX=19.8 EndY=0 EndZ=0
    g6: LineSegment StartX=19.8 StartY=0 StartZ=0 EndX=19.8 EndY=-5 EndZ=0
    g7: LineSegment StartX=19.8 StartY=-5 StartZ=0 EndX=54.8 EndY=-5 EndZ=0
  constraints (24):
    c: Coincident(g0,g1)
    c: Coincident(g1,g2)
    c: Coincident(g2,g3)
    c: Coincident(g3,g0)
    c: Horizontal(g0)
    c: Horizontal(g2)
    c: Vertical(g1)
    c: Vertical(g3)
    c: DistanceX(g2,g1) = 35
    c: DistanceX(g2,g-1) = 54.8
    c: Horizontal(g2,g-1)
    c: DistanceY(g0,g2) = 5
    c: Coincident(g4,g5)
    c: Coincident(g5,g6)
    c: Coincident(g6,g7)
    c: Coincident(g7,g4)
    c: Vertical(g4)
    c: Vertical(g6)
    c: Horizontal(g5)
    c: Horizontal(g7)
    c: Horizontal(g5,g-1)
    c: DistanceY(g4,g4) = 5
    c: DistanceX(g6,g4) = 35
    c: DistanceX(g-1,g4) = 54.8
FEATURE [PartDesign::Pad] Pad006  label="Frontplate Foot Pad"
  BaseFeature = -> Pad004
  Direction = (0,-1,2e-16)
  Length = 65
  Length2 = 3
  Placement = pos=(0,0,0) rot=(1,0,0;1.5708rad)
  Profile = -> Sketch007
  ReferenceAxis = -> Sketch007 [N_Axis]
  Suppressed = false
  Type = 4
  expr: Length = <<Monitor Chassis Parameters>>.GSBackPlateFootLengthForward
  expr: Length2 = <<Monitor Chassis Parameters>>.GSBackPlateThickness
FEATURE [Sketcher::SketchObject] Sketch008  label="Frontplate Foot Screw Holes Sketch"
  ArcFitTolerance = 1e-06
  AttachmentSupport = -> [XY_Plane002]
  FullyConstrained = true
  MakeInternals = false
  MapMode = 5
  expr: Constraints[0] = <<Monitor Chassis Parameters>>.GSBackPlateFootScrewHoleForwardOffset
  expr: Constraints[1] = 0.5 * <<Monitor Chassis Parameters>>.GSBackPlateWidth - 0.5 * <<Monitor Chassis Parameters>>.GSBackPlateFootWidth
  expr: Constraints[2] = 0.5 * <<Monitor Chassis Parameters>>.GSBackPlateWidth - 0.5 * <<Monitor Chassis Parameters>>.GSBackPlateFootWidth
  expr: Constraints[3] = <<Monitor Chassis Parameters>>.GSTowerFeetScrewDiameter
  expr: Constraints[4] = <<Monitor Chassis Parameters>>.GSTowerFeetScrewDiameter
  sketch-geometry (2):
    g0: Circle CenterX=-37.3 CenterY=-55 CenterZ=0 NormalX=0 NormalY=0 NormalZ=1 AngleXU=0 Radius=1.7
    g1: Circle CenterX=37.3 CenterY=-55 CenterZ=0 NormalX=0 NormalY=0 NormalZ=1 AngleXU=0 Radius=1.7
  constraints (6):
    c: DistanceY(g0,g-1) = 55
    c: DistanceX(g0,g-1) = 37.3
    c: DistanceX(g-1,g1) = 37.3
    c: Diameter(g0) = 3.4
    c: Diameter(g1) = 3.4
    c: Horizontal(g1,g0)
FEATURE [PartDesign::Hole] Hole001  label="Frontplate Foot Screw Holes"
  BaseFeature = -> Pad006
  CustomThreadClearance = 0
  Depth = 25
  DepthType = 0
  Diameter = 3.4
  DrillForDepth = false
  DrillPoint = 1
  DrillPointAngle = 118
  HoleCutCountersinkAngle = 90
  HoleCutCustomValues = false
  HoleCutDepth = 0
  HoleCutDiameter = 8
  HoleCutType = 2
  ModelThread = false
  Placement = pos=(0,0,0) rot=(1,0,0;1.5708rad)
  Profile = -> Sketch008
  Suppressed = false
  Tapered = false
  TaperedAngle = 90
  ThreadClass = 0
  ThreadDepth = 25
  ThreadDepthType = 0
  ThreadDirection = 0
  ThreadFit = 0
  ThreadSize = 0
  ThreadType = 0
  Threaded = false
  UseCustomThreadClearance = false
  expr: Diameter = <<Monitor Chassis Parameters>>.GSTowerFeetScrewDiameter
  expr: HoleCutDiameter = <<Monitor Chassis Parameters>>.GSM4BoltCountersinkDiameter
FEATURE [Sketcher::SketchObject] Sketch009  label="Frontplate Foot Support Corner Sketch"
  ArcFitTolerance = 1e-06
  AttachmentSupport = -> [DatumPlane001]
  FullyConstrained = true
  MakeInternals = false
  MapMode = 5
  Placement = pos=(54.8,0,0) rot=(0.57735,0.57735,0.57735;2.0944rad)
  expr: Constraints[1] = <<Monitor Chassis Parameters>>.GSBackPlateThickness
  expr: Constraints[24] = 0.8 * <<Monitor Chassis Parameters>>.GSTowerFloorDepth
  expr: Constraints[25] = 0.6 * <<Monitor Chassis Parameters>>.GSTowerFloorDepth
  expr: Constraints[26] = <<Monitor Chassis Parameters>>.GSSideCornerCutoutInset
  expr: Constraints[27] = <<Monitor Chassis Parameters>>.GSSideCornerCutoutInset
  expr: Constraints[28] = 2 * <<Monitor Chassis Parameters>>.GSSideCornerCutoutInset
  expr: Constraints[29] = 3 * <<Monitor Chassis Parameters>>.GSSideCornerCutoutInset
  expr: Constraints[39] = 0.8 * <<Monitor Chassis Parameters>>.GSTowerFloorDepth
  expr: Constraints[3] = <<Monitor Chassis Parameters>>.GSTowerFeetThickness
  expr: Constraints[41] = <<Monitor Chassis Parameters>>.GSSideCornerCutoutInset
  expr: Constraints[42] = -2 * <<Monitor Chassis Parameters>>.GSSideCornerCutoutInset
  expr: Constraints[43] = 3 * <<Monitor Chassis Parameters>>.GSSideCornerCutoutInset
  expr: Constraints[54] = 0.8 * <<Monitor Chassis Parameters>>.GSTowerFloorDepth
  expr: Constraints[55] = 0.6 * <<Monitor Chassis Parameters>>.GSTowerFloorDepth
  expr: Constraints[56] = <<Monitor Chassis Parameters>>.GSSideCornerCutoutInset
  expr: Constraints[57] = <<Monitor Chassis Parameters>>.GSSideCornerCutoutInset
  expr: Constraints[58] = 2 * <<Monitor Chassis Parameters>>.GSSideCornerCutoutInset
  expr: Constraints[59] = 3 * <<Monitor Chassis Parameters>>.GSSideCornerCutoutInset
  expr: Constraints[62] = <<Monitor Chassis Parameters>>.GSTowerThirdFloorHeight
  expr: Constraints[63] = <<Monitor Chassis Parameters>>.GSTowerSecondFloorHeight
  expr: Constraints[64] = 0.6 * <<Monitor Chassis Parameters>>.GSTowerFloorDepth
  expr: Constraints[65] = <<Monitor Chassis Parameters>>.GSTowerFourthFloorHeight + <<Monitor Chassis Parameters>>.GSTowerFloorThickness
  expr: Constraints[6] = 0.8 * <<Monitor Chassis Parameters>>.GSTowerFloorDepth
  expr: Constraints[70] = 2 * <<Monitor Chassis Parameters>>.GSSideCornerCutoutInset
  expr: Constraints[71] = 3 * <<Monitor Chassis Parameters>>.GSSideCornerCutoutInset
  expr: Constraints[73] = <<Monitor Chassis Parameters>>.GSSideCornerCutoutInset
  expr: Constraints[7] = 0.6 * <<Monitor Chassis Parameters>>.GSTowerFloorDepth
  sketch-geometry (24):
    g0: LineSegment StartX=-41 StartY=-5 StartZ=0 EndX=3 EndY=-5 EndZ=0
    g1: LineSegment StartX=3 StartY=28 StartZ=0 EndX=3 EndY=-5 EndZ=0
    g2: LineSegment StartX=-41 StartY=-5 StartZ=0 EndX=3 EndY=28 EndZ=0
    g3: LineSegment StartX=-23 StartY=171 StartZ=0 EndX=-3 EndY=186 EndZ=0
    g4: LineSegment StartX=-3 StartY=186 StartZ=0 EndX=-3 EndY=171 EndZ=0
    g5: LineSegment StartX=-23 StartY=171 StartZ=0 EndX=-3 EndY=171 EndZ=0
    g6: LineSegment StartX=3 StartY=198 StartZ=0 EndX=3 EndY=165 EndZ=0
    g7: LineSegment StartX=3 StartY=165 StartZ=0 EndX=-41 EndY=165 EndZ=0
    g8: LineSegment StartX=-41 StartY=165 StartZ=0 EndX=3 EndY=198 EndZ=0
    g9: LineSegment StartX=-23 StartY=1 StartZ=0 EndX=-3 EndY=16 EndZ=0
    g10: LineSegment StartX=-3 StartY=16 StartZ=0 EndX=-3 EndY=1 EndZ=0
    g11: LineSegment StartX=-23 StartY=1 StartZ=0 EndX=-3 EndY=1 EndZ=0
    g12: LineSegment StartX=-23 StartY=253 StartZ=0 EndX=-3 EndY=238 EndZ=0
    g13: LineSegment StartX=-3 StartY=238 StartZ=0 EndX=-3 EndY=253 EndZ=0
    g14: LineSegment StartX=-23 StartY=253 StartZ=0 EndX=-3 EndY=253 EndZ=0
    g15: LineSegment StartX=3 StartY=226 StartZ=0 EndX=3 EndY=259 EndZ=0
    g16: LineSegment StartX=3 StartY=259 StartZ=0 EndX=-41 EndY=259 EndZ=0
    g17: LineSegment StartX=-41 StartY=259 StartZ=0 EndX=3 EndY=226 EndZ=0
    g18: LineSegment StartX=-23 StartY=91 StartZ=0 EndX=-3 EndY=106 EndZ=0
    g19: LineSegment StartX=-3 StartY=106 StartZ=0 EndX=-3 EndY=91 EndZ=0
    g20: LineSegment StartX=-23 StartY=91 StartZ=0 EndX=-3 EndY=91 EndZ=0
    g21: LineSegment StartX=3 StartY=118 StartZ=0 EndX=3 EndY=85 EndZ=0
    g22: LineSegment StartX=3 StartY=85 StartZ=0 EndX=-41 EndY=85 EndZ=0
    g23: LineSegment StartX=-41 StartY=85 StartZ=0 EndX=3 EndY=118 EndZ=0
  constraints (74):
    c: Horizontal(g0)
    c: DistanceX(g-1,g0) = 3
    c: Vertical(g1)
    c: DistanceY(g0,g-1) = 5
    c: Coincident(g2,g0)
    c: Coincident(g2,g1)
    c: DistanceX(g0,g0) = 44
    c: DistanceY(g0,g1) = 33
    c: Coincident(g4,g3)
    c: Vertical(g4)
    c: Coincident(g5,g3)
    c: Coincident(g5,g4)
    c: Horizontal(g5)
    c: Vertical(g6)
    c: Coincident(g7,g6)
    c: Horizontal(g7)
    c: Coincident(g8,g7)
    c: Coincident(g8,g6)
    c: Coincident(g10,g9)
    c: Vertical(g10)
    c: Coincident(g11,g9)
    c: Coincident(g11,g10)
    c: Horizontal(g11)
    c: Vertical(g6,g1)
    c: DistanceX(g7,g6) = 44
    c: DistanceY(g6,g6) = 33
    c: DistanceY(g6,g4) = 6
    c: DistanceX(g4,g6) = 6
    c: DistanceY(g3,g6) = 12
    c: DistanceX(g7,g3) = 18
    c: Coincident(g13,g12)
    c: Vertical(g13)
    c: Coincident(g14,g12)
    c: Coincident(g14,g13)
    c: Horizontal(g14)
    c: Vertical(g15)
    c: Horizontal(g16)
    c: Coincident(g17,g16)
    c: Coincident(g17,g15)
    c: DistanceX(g16,g15) = 44
    c: DistanceY(g15,g13) = -6
    c: DistanceX(g13,g15) = 6
    c: DistanceY(g12,g15) = -12
    c: DistanceX(g16,g12) = 18
    c: Coincident(g19,g18)
    c: Vertical(g19)
    c: Coincident(g20,g18)
    c: Coincident(g20,g19)
    c: Horizontal(g20)
    c: Vertical(g21)
    c: Coincident(g22,g21)
    c: Horizontal(g22)
    c: Coincident(g23,g22)
    c: Coincident(g23,g21)
    c: DistanceX(g22,g21) = 44
    c: DistanceY(g21,g21) = 33
    c: DistanceY(g21,g19) = 6
    c: DistanceX(g19,g21) = 6
    c: DistanceY(g18,g21) = 12
    c: DistanceX(g22,g18) = 18
    c: Vertical(g21,g6)
    c: Vertical(g6,g15)
    c: DistanceY(g-1,g6) = 165
    c: DistanceY(g-1,g21) = 85
    c: DistanceY(g15,g15) = 33
    c: DistanceY(g-1,g15) = 259
    c: Horizontal(g16,g15)
    c: Vertical(g16,g15)
    c: Vertical(g1,g0)
    c: Horizontal(g1,g0)
    c: DistanceY(g9,g1) = 12
    c: DistanceX(g0,g9) = 18
    c: Vertical(g19,g9)
    c: DistanceY(g0,g10) = 6
FEATURE [PartDesign::Pad] Pad007  label="Frontplate Floor Support Corner Pad"
  BaseFeature = -> Hole001
  Direction = (1,0,0)
  Length = 2.5
  Length2 = 10
  Placement = pos=(0,0,0) rot=(1,0,0;1.5708rad)
  Profile = -> Sketch009
  ReferenceAxis = -> Sketch009 [N_Axis]
  Suppressed = false
  Type = 0
  expr: Length = <<Monitor Chassis Parameters>>.GSSideCornerThickness
FEATURE [PartDesign::Mirrored] Mirrored001  label="Frontplate Floor Support Corner Mirrored"
  BaseFeature = -> Pad007
  MirrorPlane = -> YZ_Plane002
  Originals = -> [Pad007]
  Placement = pos=(0,0,0) rot=(1,0,0;1.5708rad)
  Suppressed = false
  TransformMode = 0
FEATURE [Sketcher::SketchObject] Sketch010  label="Frontplate Floors Sketch"
  ArcFitTolerance = 1e-06
  AttachmentSupport = -> [DatumPlane001]
  FullyConstrained = true
  MakeInternals = false
  MapMode = 5
  Placement = pos=(54.8,0,0) rot=(0.57735,0.57735,0.57735;2.0944rad)
  expr: Constraints[10] = <<Monitor Chassis Parameters>>.GSTowerSecondFloorDepth
  expr: Constraints[21] = <<Monitor Chassis Parameters>>.GSTowerFourthFloorDepth
  expr: Constraints[32] = <<Monitor Chassis Parameters>>.GSTowerThirdFloorDepth
  expr: Constraints[43] = <<Monitor Chassis Parameters>>.GSTowerFirstFloorDepth
  expr: Constraints[44] = <<Monitor Chassis Parameters>>.GSTowerFirstFloorHeight
  expr: Constraints[45] = <<Monitor Chassis Parameters>>.GSTowerSecondFloorHeight
  expr: Constraints[46] = <<Monitor Chassis Parameters>>.GSTowerFourthFloorHeight
  expr: Constraints[47] = <<Monitor Chassis Parameters>>.GSTowerThirdFloorHeight
  expr: Constraints[9] = <<Monitor Chassis Parameters>>.GSTowerFloorThickness
  sketch-geometry (16):
    g0: LineSegment StartX=-55 StartY=85 StartZ=0 EndX=0 EndY=85 EndZ=0
    g1: LineSegment StartX=0 StartY=85 StartZ=0 EndX=0 EndY=89 EndZ=0
    g2: LineSegment StartX=0 StartY=89 StartZ=0 EndX=-55 EndY=89 EndZ=0
    g3: LineSegment StartX=-55 StartY=89 StartZ=0 EndX=-55 EndY=85 EndZ=0
    g4: LineSegment StartX=-55 StartY=255 StartZ=0 EndX=0 EndY=255 EndZ=0
    g5: LineSegment StartX=0 StartY=255 StartZ=0 EndX=0 EndY=259 EndZ=0
    g6: LineSegment StartX=0 StartY=259 StartZ=0 EndX=-55 EndY=259 EndZ=0
    g7: LineSegment StartX=-55 StartY=259 StartZ=0 EndX=-55 EndY=255 EndZ=0
    g8: LineSegment StartX=-55 StartY=165 StartZ=0 EndX=0 EndY=165 EndZ=0
    g9: LineSegment StartX=0 StartY=165 StartZ=0 EndX=0 EndY=169 EndZ=0
    g10: LineSegment StartX=0 StartY=169 StartZ=0 EndX=-55 EndY=169 EndZ=0
    g11: LineSegment StartX=-55 StartY=169 StartZ=0 EndX=-55 EndY=165 EndZ=0
    g12: LineSegment StartX=-50 StartY=5 StartZ=0 EndX=0 EndY=5 EndZ=0
    g13: LineSegment StartX=0 StartY=5 StartZ=0 EndX=0 EndY=9 EndZ=0
    g14: LineSegment StartX=0 StartY=9 StartZ=0 EndX=-50 EndY=9 EndZ=0
    g15: LineSegment StartX=-50 StartY=9 StartZ=0 EndX=-50 EndY=5 EndZ=0
  constraints (48):
    c: Coincident(g0,g1)
    c: Coincident(g1,g2)
    c: Coincident(g2,g3)
    c: Coincident(g3,g0)
    c: Horizontal(g0)
    c: Horizontal(g2)
    c: Vertical(g1)
    c: Vertical(g3)
    c: Vertical(g0,g-1)
    c: DistanceY(g0,g2) = 4
    c: DistanceX(g2,g1) = 55
    c: Coincident(g4,g5)
    c: Coincident(g5,g6)
    c: Coincident(g6,g7)
    c: Coincident(g7,g4)
    c: Horizontal(g4)
    c: Horizontal(g6)
    c: Vertical(g5)
    c: Vertical(g7)
    c: Vertical(g4,g-1)
    c: DistanceY(g4,g6) = 4
    c: DistanceX(g6,g5) = 55
    c: Coincident(g8,g9)
    c: Coincident(g9,g10)
    c: Coincident(g10,g11)
    c: Coincident(g11,g8)
    c: Horizontal(g8)
    c: Horizontal(g10)
    c: Vertical(g9)
    c: Vertical(g11)
    c: Vertical(g8,g-1)
    c: DistanceY(g8,g10) = 4
    c: DistanceX(g10,g9) = 55
    c: Coincident(g12,g13)
    c: Coincident(g13,g14)
    c: Coincident(g14,g15)
    c: Coincident(g15,g12)
    c: Horizontal(g12)
    c: Horizontal(g14)
    c: Vertical(g13)
    c: Vertical(g15)
    c: Vertical(g12,g-1)
    c: DistanceY(g12,g14) = 4
    c: DistanceX(g14,g13) = 50
    c: DistanceY(g-1,g12) = 5
    c: DistanceY(g-1,g0) = 85
    c: DistanceY(g-1,g4) = 255
    c: DistanceY(g-1,g8) = 165
FEATURE [PartDesign::Pad] Pad008  label="Tower Floors Pad"
  BaseFeature = -> Mirrored001
  Direction = (1,0,0)
  Length = 109.6
  Length2 = 10
  Placement = pos=(0,0,0) rot=(1,0,0;1.5708rad)
  Profile = -> Sketch010
  ReferenceAxis = -> Sketch010 [N_Axis]
  Reversed = true
  Suppressed = false
  Type = 0
  expr: Length = <<Monitor Chassis Parameters>>.GSBackPlateWidth
FEATURE [PartDesign::Plane] DatumPlane002  label="First Floor DatumPlane"
  AttachmentOffset = pos=(0,0,9) rot=(0,0,1;0rad)
  AttachmentSupport = -> [XY_Plane002]
  Length = 134.912
  MapMode = 5
  Placement = pos=(0,0,9) rot=(0,0,1;0rad)
  ResizeMode = 0
  Width = 110.312
  expr: .AttachmentOffset.Base.z = <<Monitor Chassis Parameters>>.GSTowerFirstFloorHeight + <<Monitor Chassis Parameters>>.GSTowerFloorThickness
FEATURE [PartDesign::Plane] DatumPlane003  label="Second Floor DatumPlane"
  AttachmentOffset = pos=(0,0,89) rot=(0,0,1;0rad)
  AttachmentSupport = -> [XY_Plane002]
  Length = 134.912
  MapMode = 5
  Placement = pos=(0,0,89) rot=(0,0,1;0rad)
  ResizeMode = 0
  Width = 110.312
  expr: .AttachmentOffset.Base.z = <<Monitor Chassis Parameters>>.GSTowerSecondFloorHeight + <<Monitor Chassis Parameters>>.GSTowerFloorThickness
FEATURE [PartDesign::Plane] DatumPlane004  label="Third Floor DatumPlane"
  AttachmentOffset = pos=(0,0,169) rot=(0,0,1;0rad)
  AttachmentSupport = -> [XY_Plane002]
  Length = 134.912
  MapMode = 5
  Placement = pos=(0,0,169) rot=(0,0,1;0rad)
  ResizeMode = 0
  Width = 110.312
  expr: .AttachmentOffset.Base.z = <<Monitor Chassis Parameters>>.GSTowerThirdFloorHeight + <<Monitor Chassis Parameters>>.GSTowerFloorThickness
FEATURE [Sketcher::SketchObject] Sketch011  label="Third Floor Holes Sketch"
  ArcFitTolerance = 1e-06
  AttachmentSupport = -> [DatumPlane004]
  FullyConstrained = true
  MakeInternals = false
  MapMode = 5
  Placement = pos=(0,0,169) rot=(0,0,1;0rad)
  expr: Constraints[1] = 0.5 * <<Monitor Chassis Parameters>>.GSTowerThirdFloorDepth
  expr: Constraints[2] = <<Monitor Chassis Parameters>>.GSMonitorFloorCameraMountHoleDiameter
  sketch-geometry (1):
    g0: Circle CenterX=0 CenterY=-27.5 CenterZ=0 NormalX=0 NormalY=0 NormalZ=1 AngleXU=0 Radius=2.75
  constraints (3):
    c: PointOnObject(g0,g-2)
    c: DistanceY(g0,g-1) = 27.5
    c: Diameter(g0) = 5.5
FEATURE [PartDesign::Pocket] Pocket  label="Third Floor Holes Pocket"
  BaseFeature = -> Pad008
  Direction = (0,0,-1)
  Length = 5
  Length2 = 5
  Placement = pos=(0,0,0) rot=(1,0,0;1.5708rad)
  Profile = -> Sketch011
  ReferenceAxis = -> Sketch011 [N_Axis]
  Suppressed = false
  Type = 0
FEATURE [Sketcher::SketchObject] Sketch012  label="Second Floor Holes Sketch"
  ArcFitTolerance = 1e-06
  AttachmentSupport = -> [DatumPlane003]
  FullyConstrained = true
  MakeInternals = false
  MapMode = 2
  Placement = pos=(0,0,89) rot=(0,0,1;0rad)
  expr: Constraints[0] = <<Monitor Chassis Parameters>>.GSMonitorFloorCameraMountHoleDiameter
  expr: Constraints[2] = 10 + 0.4 * <<Monitor Chassis Parameters>>.GSTowerSecondFloorDepth
  sketch-geometry (1):
    g0: Circle CenterX=0 CenterY=-32 CenterZ=0 NormalX=0 NormalY=0 NormalZ=1 AngleXU=0 Radius=2.75
  constraints (3):
    c: Diameter(g0) = 5.5
    c: Vertical(g-1,g0)
    c: DistanceY(g0,g-1) = 32
FEATURE [PartDesign::Pocket] Pocket001  label="Second Floor Holes Pocket"
  BaseFeature = -> Pocket
  Direction = (0,0,-1)
  Length = 5
  Length2 = 5
  Placement = pos=(0,0,0) rot=(1,0,0;1.5708rad)
  Profile = -> Sketch012
  ReferenceAxis = -> Sketch012 [N_Axis]
  Suppressed = false
  Type = 0
FEATURE [Sketcher::SketchObject] Sketch013  label="First Floor Holes Sketch"
  ArcFitTolerance = 1e-06
  AttachmentSupport = -> [DatumPlane002]
  FullyConstrained = true
  MakeInternals = false
  MapMode = 5
  Placement = pos=(0,0,9) rot=(0,0,1;0rad)
  expr: Constraints[0] = <<Monitor Chassis Parameters>>.GSMonitorFloorCameraMountHoleDiameter
  expr: Constraints[2] = 0.5 * <<Monitor Chassis Parameters>>.GSTowerFirstFloorDepth
  sketch-geometry (1):
    g0: Circle CenterX=0 CenterY=-25 CenterZ=0 NormalX=0 NormalY=0 NormalZ=1 AngleXU=0 Radius=2.75
  constraints (3):
    c: Diameter(g0) = 5.5
    c: Vertical(g0,g-1)
    c: DistanceY(g0,g-1) = 25
FEATURE [PartDesign::Pocket] Pocket002  label="First Floor Holes Pocket"
  BaseFeature = -> Pocket001
  Direction = (0,0,-1)
  Length = 5
  Length2 = 5
  Placement = pos=(0,0,0) rot=(1,0,0;1.5708rad)
  Profile = -> Sketch013
  ReferenceAxis = -> Sketch013 [N_Axis]
  Suppressed = false
  Type = 0
FEATURE [Sketcher::SketchObject] Sketch014  label="Shank Shield Riser Sketch"
  ArcFitTolerance = 1e-06
  AttachmentSupport = -> [XZ_Plane002]
  FullyConstrained = true
  MakeInternals = false
  MapMode = 5
  Placement = pos=(0,0,0) rot=(1,0,0;1.5708rad)
  expr: Constraints[0] = 3 * <<Monitor Chassis Parameters>>.GSM4TappingScrewHoleDiameter
  expr: Constraints[1] = <<Monitor Chassis Parameters>>.GSTowerFourthFloorHeight - 1.5 * <<Monitor Chassis Parameters>>.GSM4TappingScrewHoleDiameter
  expr: Constraints[2] = 0.5 * <<Monitor Chassis Parameters>>.GSBackPlateWidth - 1.5 * <<Monitor Chassis Parameters>>.GSM4TappingScrewHoleDiameter
  expr: Constraints[3] = 3 * <<Monitor Chassis Parameters>>.GSM4TappingScrewHoleDiameter
  expr: Constraints[5] = <<Monitor Chassis Parameters>>.GSBackPlateWidth - 3 * <<Monitor Chassis Parameters>>.GSM4TappingScrewHoleDiameter
  sketch-geometry (2):
    g0: Circle CenterX=-49.7 CenterY=249.9 CenterZ=0 NormalX=0 NormalY=0 NormalZ=1 AngleXU=0 Radius=5.1
    g1: Circle CenterX=49.7 CenterY=249.9 CenterZ=0 NormalX=0 NormalY=0 NormalZ=1 AngleXU=0 Radius=5.1
  constraints (6):
    c: Diameter(g0) = 10.2
    c: DistanceY(g-1,g0) = 249.9
    c: DistanceX(g0,g-1) = 49.7
    c: Diameter(g1) = 10.2
    c: Horizontal(g0,g1)
    c: DistanceX(g0,g1) = 99.4
FEATURE [PartDesign::Pad] Pad009  label="Shank Shield Riser Pad"
  BaseFeature = -> Pocket002
  Direction = (0,-1,2e-16)
  Length = 97.65
  Length2 = 10
  Placement = pos=(0,0,0) rot=(1,0,0;1.5708rad)
  Profile = -> Sketch014
  ReferenceAxis = -> Sketch014 [N_Axis]
  Suppressed = false
  Type = 0
  expr: Length = 1 + <<Monitor Chassis Parameters>>.GSBasePowerBoxTowerBackOffsetFromFront - <<Monitor Chassis Parameters>>.GSShankShieldThickness - <<Monitor Chassis Parameters>>.GSBackPlateThickness - <<Monitor Chassis Parameters>>.GSBasePowerBoxSideThickness
FEATURE [PartDesign::Plane] DatumPlane005  label="Shank Shield Riser Front DatumPlane005"
  AttachmentSupport = -> [Pad009]
  Length = 150.681
  MapMode = 5
  Placement = pos=(0,-97.65,0) rot=(1,0,0;1.5708rad)
  ResizeMode = 0
  Width = 320.081
FEATURE [Sketcher::SketchObject] Sketch015  label="Shank Shield Riser Screw Holes Sketch"
  ArcFitTolerance = 1e-06
  AttachmentSupport = -> [DatumPlane005]
  FullyConstrained = true
  MakeInternals = false
  MapMode = 5
  Placement = pos=(0,-97.65,0) rot=(1,0,0;1.5708rad)
  expr: Constraints[0] = 0.5 * <<Monitor Chassis Parameters>>.GSBackPlateWidth - 1.5 * <<Monitor Chassis Parameters>>.GSM4TappingScrewHoleDiameter
  expr: Constraints[1] = <<Monitor Chassis Parameters>>.GSM4TappingScrewHoleDiameter
  expr: Constraints[3] = <<Monitor Chassis Parameters>>.GSTowerFourthFloorHeight - 1.5 * <<Monitor Chassis Parameters>>.GSM4TappingScrewHoleDiameter
  expr: Constraints[4] = 0.5 * <<Monitor Chassis Parameters>>.GSBackPlateWidth - 1.5 * <<Monitor Chassis Parameters>>.GSM4TappingScrewHoleDiameter
  expr: Constraints[5] = <<Monitor Chassis Parameters>>.GSM4TappingScrewHoleDiameter
  sketch-geometry (2):
    g0: Circle CenterX=-49.7 CenterY=249.9 CenterZ=0 NormalX=0 NormalY=0 NormalZ=1 AngleXU=0 Radius=1.7
    g1: Circle CenterX=49.7 CenterY=249.9 CenterZ=0 NormalX=0 NormalY=0 NormalZ=1 AngleXU=0 Radius=1.7
  constraints (6):
    c: DistanceX(g0,g-1) = 49.7
    c: Diameter(g0) = 3.4
    c: Horizontal(g0,g1)
    c: DistanceY(g-1,g0) = 249.9
    c: DistanceX(g-1,g1) = 49.7
    c: Diameter(g1) = 3.4
FEATURE [PartDesign::Pocket] Pocket003  label="Shank Shield Riser Screw Holes Pocket"
  BaseFeature = -> Pad009
  Direction = (0,1,-2e-16)
  Length = 14
  Length2 = 5
  Placement = pos=(0,0,0) rot=(1,0,0;1.5708rad)
  Profile = -> Sketch015
  ReferenceAxis = -> Sketch015 [N_Axis]
  Suppressed = false
  Type = 0
  expr: Length = 14
FEATURE [PartDesign::Plane] DatumPlane006  label="Fourth Floor DatumPlane"
  AttachmentOffset = pos=(0,0,259) rot=(0,0,1;0rad)
  AttachmentSupport = -> [XY_Plane002]
  Length = 134.912
  MapMode = 5
  Placement = pos=(0,0,259) rot=(0,0,1;0rad)
  ResizeMode = 0
  Width = 110.312
  expr: .AttachmentOffset.Base.z = <<Monitor Chassis Parameters>>.GSTowerFourthFloorHeight + <<Monitor Chassis Parameters>>.GSTowerFloorThickness
FEATURE [Sketcher::SketchObject] Sketch016  label="Fourth Floor Cutout Sketch"
  ArcFitTolerance = 1e-06
  AttachmentSupport = -> [DatumPlane006]
  FullyConstrained = false
  MakeInternals = false
  MapMode = 5
  Placement = pos=(0,0,259) rot=(0,0,1;0rad)
  sketch-geometry (4):
    g0: LineSegment StartX=-44.9421 StartY=-8.20433 StartZ=0 EndX=-44.9421 EndY=-45.1974 EndZ=0
    g1: LineSegment StartX=-44.9421 StartY=-45.1974 StartZ=0 EndX=49.6477 EndY=-45.1974 EndZ=0
    g2: LineSegment StartX=49.6477 StartY=-45.1974 StartZ=0 EndX=49.6477 EndY=-8.20433 EndZ=0
    g3: LineSegment StartX=49.6477 StartY=-8.20433 StartZ=0 EndX=-44.9421 EndY=-8.20433 EndZ=0
  constraints (8):
    c: Coincident(g0,g1)
    c: Coincident(g1,g2)
    c: Coincident(g2,g3)
    c: Coincident(g3,g0)
    c: Vertical(g0)
    c: Vertical(g2)
    c: Horizontal(g1)
    c: Horizontal(g3)
FEATURE [PartDesign::Plane] DatumPlane007  label="Suggested Backplate Split DatumPlane"
  AttachmentOffset = pos=(0,0,102) rot=(0,0,1;0rad)
  AttachmentSupport = -> [XY_Plane001]
  Length = 130.764
  MapMode = 5
  Placement = pos=(0,0,102) rot=(0,0,1;0rad)
  ResizeMode = 0
  Width = 73.1644
  expr: .AttachmentOffset.Base.z = 102
FEATURE [PartDesign::Plane] DatumPlane008  label="Suggested Frontplate Split DatumPlane"
  AttachmentOffset = pos=(0,0,145) rot=(0,0,1;0rad)
  AttachmentSupport = -> [XY_Plane002]
  Length = 134.912
  MapMode = 5
  Placement = pos=(0,0,145) rot=(0,0,1;0rad)
  ResizeMode = 0
  Width = 110.312
FEATURE [PartDesign::Body] Body001  label="Frontplate Body (same as other variant)"
  AllowCompound = false
  Group = -> [Sketch005,Pad004,Sketch007,Pad006,Sketch008,Hole001,DatumPlane001,Sketch009,Pad007,Mirrored001,Sketch010,Pad008,DatumPlane002,DatumPlane003,DatumPlane004,Sketch011,Pocket,Sketch012,Pocket001,Sketch013,Pocket002,Sketch014,Pad009,DatumPlane005,Sketch015,Pocket003,DatumPlane006,Sketch016,DatumPlane008]
  Origin = -> Origin002
  Placement = pos=(0.1,5,0) rot=(0,0,1;3.14159rad)
  Tip = -> Pocket003
FEATURE [Sketcher::SketchObject] Sketch017  label="Tower Layer Join Screw Holes Sketch"
  ArcFitTolerance = 1e-06
  AttachmentSupport = -> [XZ_Plane001]
  FullyConstrained = true
  MakeInternals = false
  MapMode = 5
  Placement = pos=(0,0,0) rot=(1,0,0;1.5708rad)
  expr: Constraints[0] = <<Monitor Chassis Parameters>>.GSTowerLayerJoinScrewDiameter
  expr: Constraints[1] = <<Monitor Chassis Parameters>>.GSM2TappingScrewHoleDiameter
  expr: Constraints[22] = 0.5 * <<Monitor Chassis Parameters>>.GSBackPlateWidth - <<Monitor Chassis Parameters>>.GSTowerLayerJoinScrewInset
  expr: Constraints[23] = 0.5 * <<Monitor Chassis Parameters>>.GSBackPlateWidth - <<Monitor Chassis Parameters>>.GSTowerLayerJoinScrewInset
  expr: Constraints[24] = <<Monitor Chassis Parameters>>.GSTowerLayerJoinScrewHeightFromFoot_1
  expr: Constraints[25] = <<Monitor Chassis Parameters>>.GSTowerLayerJoinScrewHeightFromFoot_2
  expr: Constraints[26] = <<Monitor Chassis Parameters>>.GSTowerLayerJoinScrewHeightFromFoot_3
  expr: Constraints[27] = <<Monitor Chassis Parameters>>.GSTowerLayerJoinScrewHeightFromFoot_4
  expr: Constraints[28] = <<Monitor Chassis Parameters>>.GSTowerLayerJoinScrewHeightFromFoot_5
  expr: Constraints[29] = <<Monitor Chassis Parameters>>.GSM2TappingScrewHoleDiameter
  expr: Constraints[2] = <<Monitor Chassis Parameters>>.GSM2TappingScrewHoleDiameter
  expr: Constraints[30] = <<Monitor Chassis Parameters>>.GSM2TappingScrewHoleDiameter
  expr: Constraints[35] = <<Monitor Chassis Parameters>>.GSTowerLayerJoinScrewHeightFromFoot_6
  expr: Constraints[3] = <<Monitor Chassis Parameters>>.GSM2TappingScrewHoleDiameter
  expr: Constraints[4] = <<Monitor Chassis Parameters>>.GSM2TappingScrewHoleDiameter
  expr: Constraints[5] = <<Monitor Chassis Parameters>>.GSM2TappingScrewHoleDiameter
  expr: Constraints[6] = <<Monitor Chassis Parameters>>.GSM2TappingScrewHoleDiameter
  expr: Constraints[7] = <<Monitor Chassis Parameters>>.GSM2TappingScrewHoleDiameter
  expr: Constraints[8] = <<Monitor Chassis Parameters>>.GSM2TappingScrewHoleDiameter
  expr: Constraints[9] = <<Monitor Chassis Parameters>>.GSM2TappingScrewHoleDiameter
  sketch-geometry (12):
    g0: Circle CenterX=44.8 CenterY=157 CenterZ=0 NormalX=0 NormalY=0 NormalZ=1 AngleXU=0 Radius=0.855
    g1: Circle CenterX=-44.8 CenterY=135 CenterZ=0 NormalX=0 NormalY=0 NormalZ=1 AngleXU=0 Radius=0.855
    g2: Circle CenterX=44.8 CenterY=135 CenterZ=0 NormalX=0 NormalY=0 NormalZ=1 AngleXU=0 Radius=0.855
    g3: Circle CenterX=-44.8 CenterY=112 CenterZ=0 NormalX=0 NormalY=0 NormalZ=1 AngleXU=0 Radius=0.855
    g4: Circle CenterX=-44.8 CenterY=94 CenterZ=0 NormalX=0 NormalY=0 NormalZ=1 AngleXU=0 Radius=0.855
    g5: Circle CenterX=44.8 CenterY=112 CenterZ=0 NormalX=0 NormalY=0 NormalZ=1 AngleXU=0 Radius=0.855
    g6: Circle CenterX=44.8 CenterY=94 CenterZ=0 NormalX=0 NormalY=0 NormalZ=1 AngleXU=0 Radius=0.855
    g7: Circle CenterX=-44.8 CenterY=30 CenterZ=0 NormalX=0 NormalY=0 NormalZ=1 AngleXU=0 Radius=0.855
    g8: Circle CenterX=44.8 CenterY=30 CenterZ=0 NormalX=0 NormalY=0 NormalZ=1 AngleXU=0 Radius=0.855
    g9: Circle CenterX=-44.8 CenterY=157 CenterZ=0 NormalX=0 NormalY=0 NormalZ=1 AngleXU=0 Radius=0.855
    g10: Circle CenterX=-44.8 CenterY=230 CenterZ=0 NormalX=0 NormalY=0 NormalZ=1 AngleXU=0 Radius=0.855
    g11: Circle CenterX=44.8 CenterY=230 CenterZ=0 NormalX=0 NormalY=0 NormalZ=1 AngleXU=0 Radius=0.855
  constraints (36):
    c: Diameter(g0) = 1.71
    c: Diameter(g1) = 1.71
    c: Diameter(g2) = 1.71
    c: Diameter(g3) = 1.71
    c: Diameter(g4) = 1.71
    c: Diameter(g5) = 1.71
    c: Diameter(g6) = 1.71
    c: Diameter(g7) = 1.71
    c: Diameter(g8) = 1.71
    c: Diameter(g9) = 1.71
    c: Vertical(g9,g1)
    c: Vertical(g1,g3)
    c: Vertical(g4,g3)
    c: Vertical(g7,g4)
    c: Vertical(g8,g6)
    c: Vertical(g6,g5)
    c: Vertical(g5,g2)
    c: Vertical(g0,g2)
    c: Horizontal(g2,g1)
    c: Horizontal(g3,g5)
    c: Horizontal(g4,g6)
    c: Horizontal(g7,g8)
    c: DistanceX(g7,g-1) = 44.8
    c: DistanceX(g-1,g8) = 44.8
    c: DistanceY(g-1,g7) = 30
    c: DistanceY(g-1,g4) = 94
    c: DistanceY(g-1,g3) = 112
    c: DistanceY(g-1,g1) = 135
    c: DistanceY(g-1,g9) = 157
    c: Diameter(g11) = 1.71
    c: Diameter(g10) = 1.71
    c: Horizontal(g9,g0)
    c: Vertical(g0,g11)
    c: Horizontal(g10,g11)
    c: Vertical(g10,g9)
    c: DistanceY(g-1,g10) = 230
FEATURE [PartDesign::Hole] Hole002  label="Plate Connection Holes"
  BaseFeature = -> Mirrored
  CustomThreadClearance = 0
  Depth = 25
  DepthType = 0
  Diameter = 1.71
  DrillForDepth = false
  DrillPoint = 1
  DrillPointAngle = 118
  HoleCutCountersinkAngle = 90
  HoleCutCustomValues = false
  HoleCutDepth = 0
  HoleCutDiameter = 3.5
  HoleCutType = 2
  ModelThread = false
  Placement = pos=(0,0,0) rot=(1,0,0;1.5708rad)
  Profile = -> Sketch017
  Suppressed = false
  Tapered = false
  TaperedAngle = 90
  ThreadClass = 0
  ThreadDepth = 25
  ThreadDepthType = 0
  ThreadDirection = 0
  ThreadFit = 0
  ThreadSize = 0
  ThreadType = 0
  Threaded = false
  UseCustomThreadClearance = false
  expr: Diameter = <<Monitor Chassis Parameters>>.GSTowerLayerJoinScrewDiameter
  expr: HoleCutDiameter = <<Monitor Chassis Parameters>>.GSM2BoltCountersinkDiameter
FEATURE [PartDesign::Body] Body  label="Backplate Body - Connector Board Variant"
  AllowCompound = false
  Group = -> [Sketch,Sketch001,Pad,Pad001,Sketch002,Pad002,Sketch003,Hole,DatumPlane,Sketch004,Pad003,Mirrored,DatumPlane007,Sketch017,Hole002]
  Origin = -> Origin001
  Placement = pos=(0.2,-1,0) rot=(0,0,1;0rad)
  Tip = -> Hole002
FEATURE [App::Part] Part  label="Tower Part"
  Group = -> [Body,Body001]
  Origin = -> Origin
FEATURE [App::Link] Link001  label="GolfSim Connector Board 1"
  LinkPlacement = pos=(-142.5,-11.983,231.958) rot=(1,0,0;1.5708rad)
  LinkedObject = -> <external ../../../Dev/PiTrac/3D Printed Parts/Enclosure Models/Combined Enclosure Model (DO NOT PRINT)/Connector Board.FCStd>#GolfSim_Connector_Board_1
  Placement = pos=(-142.5,-11.983,231.958) rot=(1,0,0;1.5708rad)
FEATURE [App::Link] Link002  label="RASPBERRY_PI_5_1"
  LinkPlacement = pos=(-5.9,-12.4001,219) rot=(1,0,0;3.14159rad)
  LinkedObject = -> <external ../../../Dev/PiTrac/3D Printed Parts/Enclosure Models/Combined Enclosure Model (DO NOT PRINT)/Pi 5.FCStd>#RASPBERRY_PI_5_1
  Placement = pos=(-5.9,-12.4001,219) rot=(1,0,0;3.14159rad)
